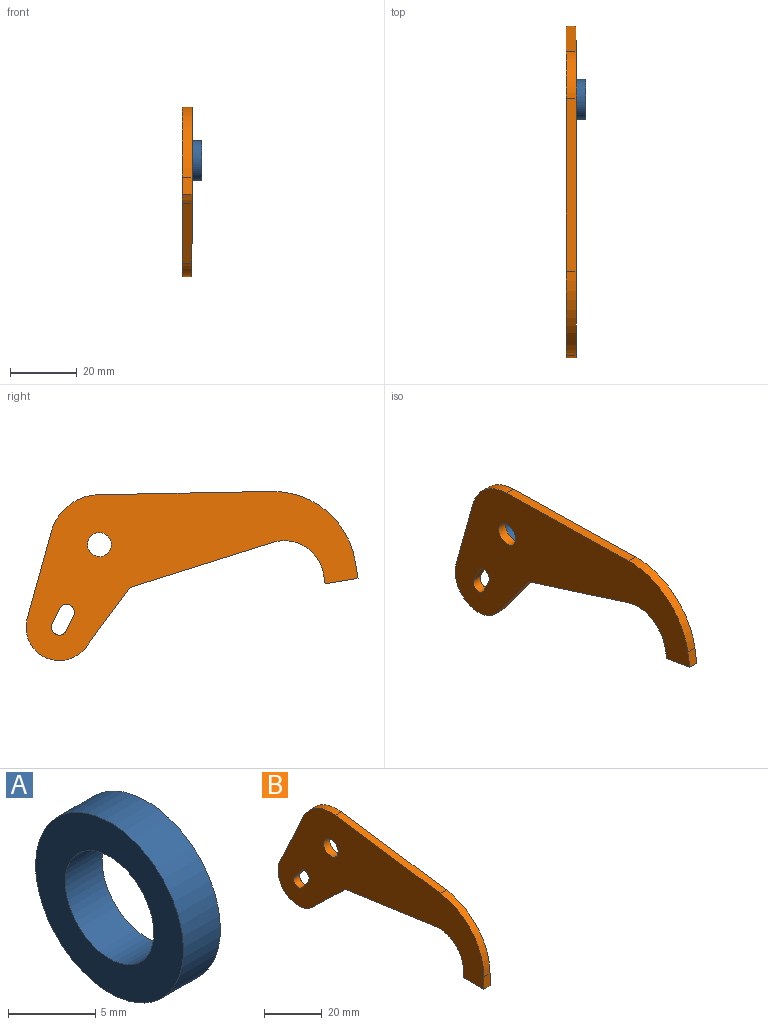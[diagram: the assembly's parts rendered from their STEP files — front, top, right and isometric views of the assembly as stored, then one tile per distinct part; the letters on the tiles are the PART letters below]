
ASSEMBLY  parts=2 mates=1
PART A: 4 faces, bbox 3x12x12 mm
  f0: plane 12x12mm, normal (1,0,0), area 72.4mm2, adj f1,f2
  f1: cylinder r=3.6mm len=7.2mm, axis (-1,0,0), area 67.9mm2, adj f0,f3
  f2: cylinder r=6mm len=12mm, axis (-1,0,0), area 113.1mm2, adj f0,f3
  f3: plane 12x12mm, normal (-1,0,0), area 72.4mm2, adj f1,f2
PART B: 18 faces, bbox 3x101x47.6 mm
  f0: plane 100.95x47.55mm, normal (1,0,0), area 2358.5mm2, adj f1,f2,f3,f4,f5,f6,f7,f8
  f1: cylinder r=2.35mm len=4.27mm, axis (-1,0,0), area 22.1mm2, adj f0,f2,f16,f17
  f2: plane 4.14x3mm, normal (0,0.82,0.58), area 15.2mm2, adj f0,f1,f3,f17
  f3: cylinder r=2.35mm len=4.27mm, axis (-1,0,0), area 22.1mm2, adj f0,f2,f16,f17
  f4: plane 44.31x6.4mm, normal (0,-0.14,-0.99), area 134.3mm2, adj f0,f5,f15,f17
  f5: plane 15.95x15.56mm, normal (0,-0.7,-0.72), area 66.8mm2, adj f0,f4,f6,f17
  f6: cylinder r=10mm len=16.98mm, axis (-1,0,0), area 83.3mm2, adj f0,f5,f7,f17
  f7: plane 24.65x11.41mm, normal (0,0.91,0.42), area 81.5mm2, adj f0,f6,f8,f17
  f8: cylinder r=15mm len=15.75mm, axis (-1,0,0), area 57.6mm2, adj f0,f7,f9,f17
  f9: plane 51.43x7.42mm, normal (0,-0.14,0.99), area 155.9mm2, adj f0,f8,f10,f17
  f10: cylinder r=25mm len=24.74mm, axis (-1,0,0), area 107.1mm2, adj f0,f9,f11,f17
  f11: plane 5.23x3mm, normal (0,-1,0), area 15.7mm2, adj f0,f10,f12,f17
  f12: plane 10x3mm, normal (0,0,-1), area 30mm2, adj f0,f11,f13,f17
  f13: plane 3x2.92mm, normal (0,1,0), area 8.8mm2, adj f0,f12,f15,f17
  f14: cylinder r=3.6mm len=7.2mm, axis (-1,0,0), area 67.9mm2, adj f0,f17
  f15: cylinder r=12mm len=13.71mm, axis (-1,0,0), area 61.7mm2, adj f0,f4,f13,f17
  f16: plane 4.14x3mm, normal (0,-0.82,-0.58), area 15.2mm2, adj f0,f1,f3,f17
  f17: plane 100.95x47.55mm, normal (-1,0,0), area 2358.5mm2, adj f1,f2,f3,f4,f5,f6,f7,f8
PLACE A rot(axis=(-1,0,0),9.3deg) t=(-11.3,29.66,34.72)mm
PLACE B rot(axis=(-1,0,0),9.3deg) t=(-11.3,29.66,34.72)mm
MATE fastened B.f8 <-> A.f1  axis (1,0,0) through (3.7,9.72,60.84)mm
